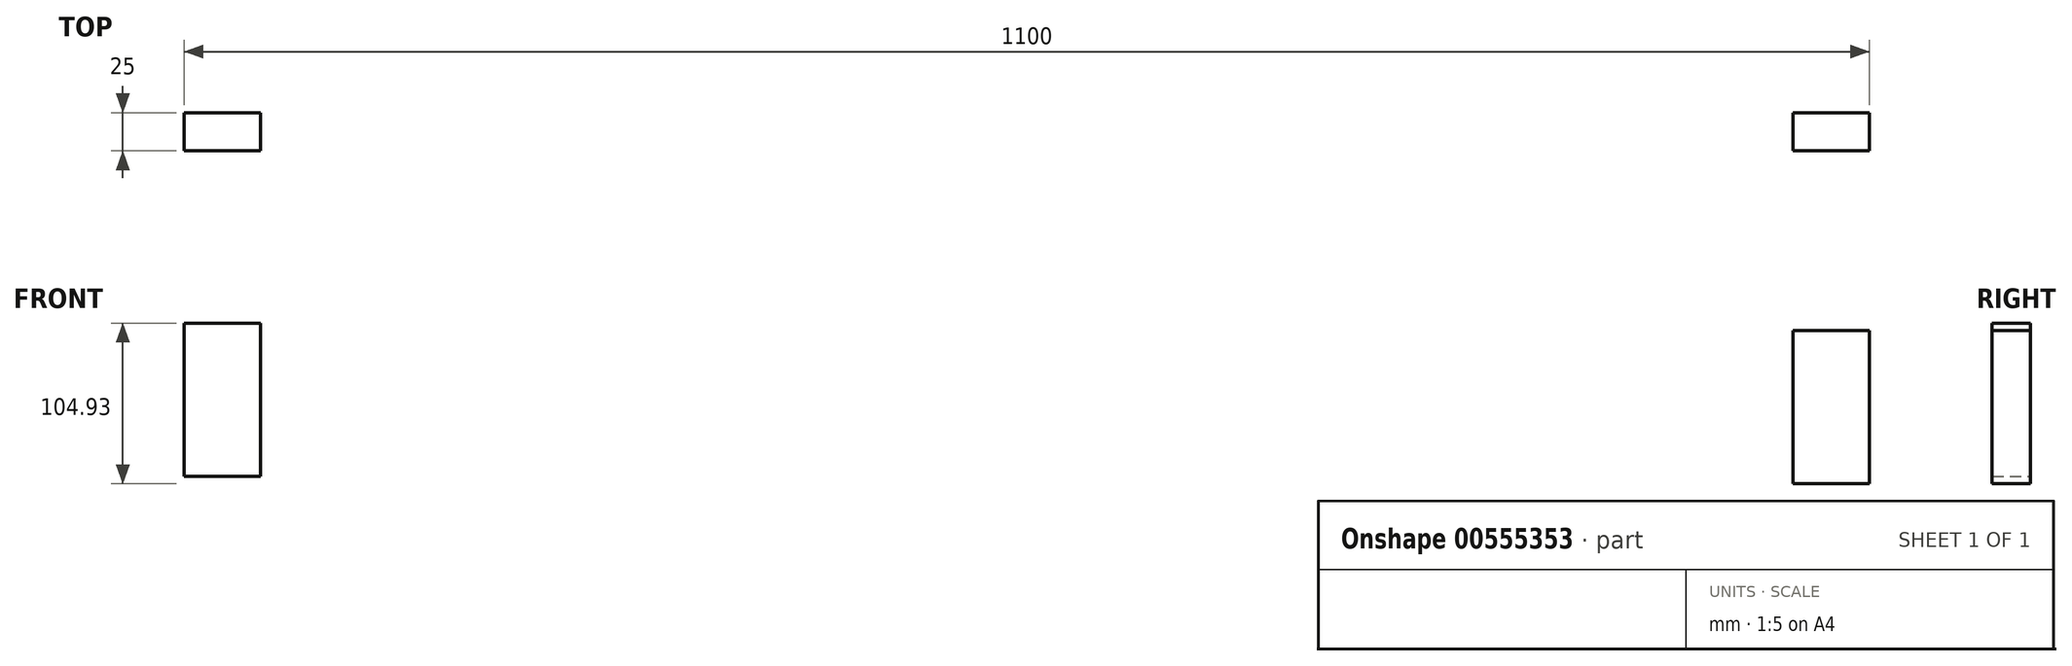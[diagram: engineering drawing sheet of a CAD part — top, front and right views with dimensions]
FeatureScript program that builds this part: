
annotation { "Feature Type Name" : "Feature", "Feature Type Description" : "" }
export const myFeature = defineFeature(function(context is Context, id is Id, definition is map)
    precondition{}
    {
        {
            var Q0;
            Q0=qCreatedBy(makeId("Front.planeOp"),FACE);
            var sketch = newSketch(context, id + "F0", { "sketchPlane" : qUnion([Q0])});
            skLineSegment(sketch, "E0.bottom", {"start": v(-654.6, -81.68) * mm, "end": v(-704.6, -81.68) * mm});
            skLineSegment(sketch, "E0.top", {"start": v(-654.6, -181.68) * mm, "end": v(-704.6, -181.68) * mm});
            skLineSegment(sketch, "E0.left", {"start": v(-654.6, -81.68) * mm, "end": v(-654.6, -181.68) * mm});
            skLineSegment(sketch, "E0.right", {"start": v(-704.6, -81.68) * mm, "end": v(-704.6, -181.68) * mm});
            skLineSegment(sketch, "E1.bottom", {"start": v(395.4, -86.6) * mm, "end": v(345.4, -86.6) * mm});
            skLineSegment(sketch, "E1.top", {"start": v(395.4, -186.6) * mm, "end": v(345.4, -186.6) * mm});
            skLineSegment(sketch, "E1.left", {"start": v(395.4, -86.6) * mm, "end": v(395.4, -186.6) * mm});
            skLineSegment(sketch, "E1.right", {"start": v(345.4, -86.6) * mm, "end": v(345.4, -186.6) * mm});
            skSolve(sketch);
        }
        {
            var Q0;
            Q0 = qSketchRegion(id + "F0", true);
            extrude(context, id + "F1", {"entities" : qUnion([Q0]), "depth" : 25 * mm, "offsetDistance" : 25 * mm});
        }
    });
